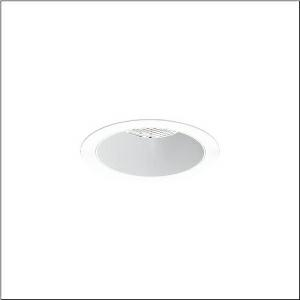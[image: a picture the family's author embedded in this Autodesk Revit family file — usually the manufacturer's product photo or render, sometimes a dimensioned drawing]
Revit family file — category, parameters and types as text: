
# Revit family: lunis_21_l_51db18md91c
name_source: partatom
category: Lighting Fixtures
units: mm (PartAtom-declared; Revit-internal decimal feet)

## family parameters
Cut with Voids When Loaded = No
Host = Face
Light Source = No
Part Type = Normal
Room Calculation Point = No
Round Connector Dimension = Use Diameter
Shared = No

## types (1)
- --- (1 x LED, 3560 lm, 21.7 W, 6500K)
    Apparent Load = 22 VA
    CIE Flux Codes = 87 97 99 100 100
    Color Rendering = 80
    Color Temperature = 6500K
    Default Elevation = 1800 mm
    Description = Lunis 21 L, downlight, light control with lens, of PMMA, anti glare with reflector, of PC, light emission: direct distribution, LED rated luminous flux: 2.160lm, light colour: 830/840/865, with terminal, 3-pole, mains connection: 220..240V, AC/DC, 0/50..60Hz, housing, round, of diecast aluminium, traffic white (RAL 9016), diameter: 165mm, clamping range: 1..40mm, protection rating (complete): IP20, protection rating (on room side): IP54, insulation class (complete): insulation class II (safety insulation), certification: CE, impact resistance: IK03, packaging unit: 1 piece
    Height = 0 mm  [stored 0 ft]
    Lamp = 1 x LED
    Lamp Light Flux = 3560 lm
    Lamp Power = 21.7 W
    Lamp count = 1
    Length = 165 mm
    Luminous efficacy = 164 lm/W
    Manufacturer = Siteco
    ModVariant = No
    Model = 51DB18MD91C
    Mounting Place = Ceiling
    Mounting Type = Recessed
    Number of Poles = 1
    OnlyDefault = Yes
    Power Factor = 1
    Product Name = Lunis 21 L
    Product group = downlight
    ProductGroupID = 401
    Protection Class = Protection class II
    Protection Degree = IP 20
    RLX_Detail_Level = 1
    RLX_Emergency_Light_Flux = 0 lm
    RLX_Emergency_Type = 0
    RLX_Emergency_Type_DB = No
    RlxData = <blob elided: 14745 chars, md5=97269b05>
    Socket = socket
    Standby Power = 0 W
    System Light Flux = 3560 lm
    System Power = 22 W
    Type Comments = individual setting: colour temperature 6500K, luminous flux: 100 % | (OFF | ON | ON | ON) | 650 mA
    Type Image = l_1291155.jpg
    URL = http://relux.com
    VarID = @adj_035319
    Voltage = 0 V
    Weight = 0.00 kg
    Width = 0 mm  [stored 0 ft]

note: [stored X ft] marks values corroborated as IEEE doubles in the binary element streams (Revit-internal decimal feet)

## geometry (parser evidence)
native form markers: Sweep x11
no freeform markers — native parametric forms only
